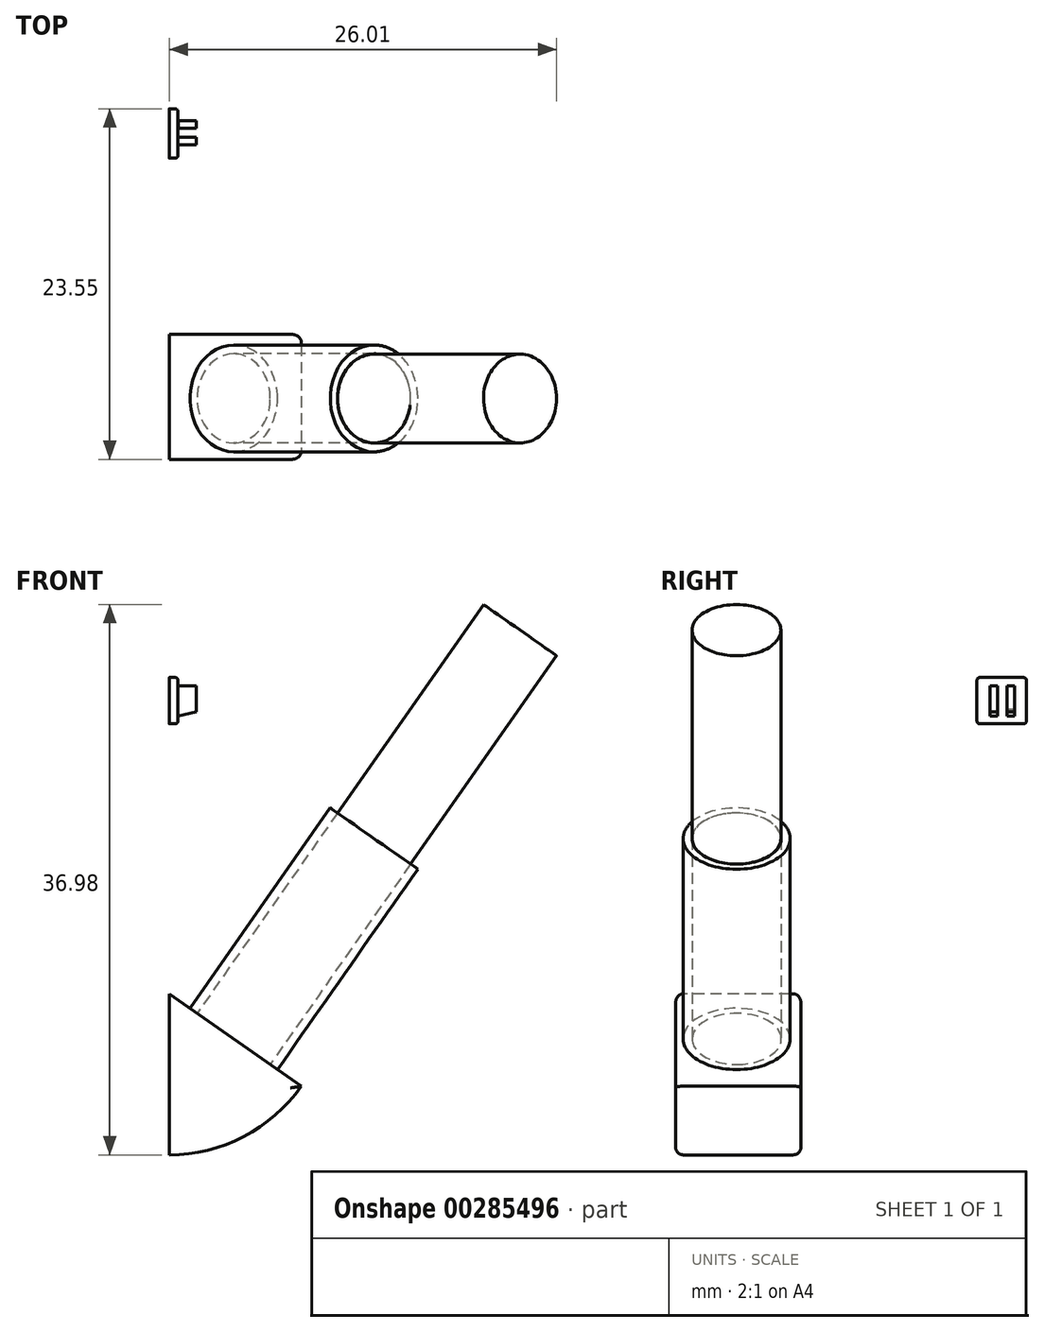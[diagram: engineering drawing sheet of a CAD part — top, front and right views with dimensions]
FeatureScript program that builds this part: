
annotation { "Feature Type Name" : "Feature", "Feature Type Description" : "" }
export const myFeature = defineFeature(function(context is Context, id is Id, definition is map)
    precondition{}
    {
        {
            var Q0;
            Q0=qCreatedBy(makeId("Right.planeOp"),FACE);
            var sketch = newSketch(context, id + "F0", { "sketchPlane" : qUnion([Q0])});
            skLineSegment(sketch, "E0.bottom", {"start": v(-51.68, 34.1) * mm, "end": v(-60.1, 34.1) * mm});
            skLineSegment(sketch, "E0.top", {"start": v(-51.68, 44.92) * mm, "end": v(-60.1, 44.92) * mm});
            skLineSegment(sketch, "E0.left", {"start": v(-51.68, 34.1) * mm, "end": v(-51.68, 44.92) * mm});
            skLineSegment(sketch, "E0.right", {"start": v(-60.1, 34.1) * mm, "end": v(-60.1, 44.92) * mm});
            skPoint(sketch, "E0.middle", {"position": v(-55.89, 39.5) * mm});
            skSolve(sketch);
        }
        {
            var Q0;
            Q0=makeQuery(id+"F0.imprint","IMPRINT",FACE,{"disambiguationData":[TD([[makeQuery(id+"F0.imprint","IMPRINT",EDGE,{"derivedFrom":sQuery(id+"F0.wireOp",EDGE,"E0.bottom")}),-1.0]])]});
            var Q1;
            Q1=sQuery(id+"F0.wireOp",EDGE,"E0.top");
            revolve(context, id + "F1", {"entities" : qUnion([Q0]), "axis" : qUnion([Q1]), "revolveType" : RevolveType.ONE_DIRECTION, "angle" : 55 * degree});
        }
        {
            var Q0;
            Q0=makeQuery(id+"F1.opRevolve","CAP_FACE",FACE,{"disambiguationData":[OSD([sQuery(id+"F0.wireOp",EDGE,"E0.bottom"),sQuery(id+"F0.wireOp",EDGE,"E0.top"),sQuery(id+"F0.wireOp",EDGE,"E0.left"),sQuery(id+"F0.wireOp",EDGE,"E0.right")])],"isStart":false});
            var sketch = newSketch(context, id + "F2", { "sketchPlane" : qUnion([Q0])});
            skCircle(sketch, "E1", {"center": v(-20.48, -55.99) * mm, "radius": 3.59 * mm});
            skCircle(sketch, "E2", {"center": v(-20.48, -55.99) * mm, "radius": 3 * mm});
            skSolve(sketch);
        }
        {
            var Q0;
            Q0=makeQuery(id+"F2.imprint","IMPRINT",FACE,{"disambiguationData":[TD([[makeQuery(id+"F2.imprint","IMPRINT",EDGE,{"derivedFrom":sQuery(id+"F2.wireOp",EDGE,"E1")}),1.0]])]});
            extrude(context, id + "F3", {"entities" : qUnion([Q0]), "operationType" : NewBodyOperationType.ADD, "depth" : 16.43 * mm});
        }
        {
            var Q0;
            Q0=makeQuery(id+"F3.opExtrude","CAP_FACE",FACE,{"disambiguationData":[OSD([sQuery(id+"F2.wireOp",EDGE,"E1"),sQuery(id+"F2.wireOp",EDGE,"E2")])],"isStart":false});
            var sketch = newSketch(context, id + "F4", { "sketchPlane" : qUnion([Q0])});
            skCircle(sketch, "E3", {"center": v(-20.48, -56.01) * mm, "radius": 3 * mm});
            skSolve(sketch);
        }
        {
            var Q0;
            {var subQ0=sQuery(id+"F4.wireOp",EDGE,"E3");var subQ1=makeQuery(id+"F3.opExtrude","CAP_EDGE",EDGE,{"disambiguationData":[OSD([sQuery(id+"F2.wireOp",EDGE,"E2")])],"isStart":false});var subQ2=makeQuery(id+"F4.imprint","INTERSECT",VERTEX,{"disambiguationData":[OD(0.0)],"derivedFrom":[subQ1,subQ0]});Q0=makeQuery(id+"F4.imprint","IMPRINT",FACE,{"disambiguationData":[TD([[makeQuery(id+"F4.imprint","IMPRINT",EDGE,{"disambiguationData":[TD([[subQ2,1.0]])],"derivedFrom":subQ0}),1.0]])]});}
            var Q1;
            Q1=sQuery(id+"F4.wireOp",EDGE,"E3");
            extrude(context, id + "F5", {"entities" : qUnion([Q0]), "surfaceEntities" : qUnion([Q1]), "depth" : 17.1 * mm});
        }
        {
            var Q0;
            Q0=qCreatedBy(makeId("Right.planeOp"),FACE);
            var sketch = newSketch(context, id + "F6", { "sketchPlane" : qUnion([Q0])});
            skCircle(sketch, "E4", {"center": v(-38.2, 64.6) * mm, "radius": 3 * mm});
            skLineSegment(sketch, "E5.bottom", {"start": v(-36.54, 63.05) * mm, "end": v(-39.85, 63.05) * mm});
            skLineSegment(sketch, "E5.top", {"start": v(-36.54, 66.16) * mm, "end": v(-39.85, 66.16) * mm});
            skLineSegment(sketch, "E5.left", {"start": v(-36.54, 63.05) * mm, "end": v(-36.54, 66.16) * mm});
            skLineSegment(sketch, "E5.right", {"start": v(-39.85, 63.05) * mm, "end": v(-39.85, 66.16) * mm});
            skSolve(sketch);
        }
        {
            var Q0;
            Q0=makeQuery(id+"F6.imprint","IMPRINT",FACE,{"disambiguationData":[TD([[makeQuery(id+"F6.imprint","IMPRINT",EDGE,{"derivedFrom":sQuery(id+"F6.wireOp",EDGE,"E5.bottom")}),-1.0]])]});
            extrude(context, id + "F7", {"entities" : qUnion([Q0]), "depth" : 0.58 * mm});
        }
        {
            var Q0;
            Q0=makeQuery(id+"F7.opExtrude","SWEPT_EDGE",EDGE,{"disambiguationData":[OSD([sQuery(id+"F6.wireOp",EDGE,"E5.top"),sQuery(id+"F6.wireOp",EDGE,"E5.right")])]});
            var Q1;
            Q1=makeQuery(id+"F7.opExtrude","SWEPT_EDGE",EDGE,{"disambiguationData":[OSD([sQuery(id+"F6.wireOp",EDGE,"E5.top"),sQuery(id+"F6.wireOp",EDGE,"E5.left")])]});
            var Q2;
            Q2=makeQuery(id+"F7.opExtrude","CAP_FACE",FACE,{"disambiguationData":[OSD([sQuery(id+"F6.wireOp",EDGE,"E5.bottom"),sQuery(id+"F6.wireOp",EDGE,"E5.top"),sQuery(id+"F6.wireOp",EDGE,"E5.left"),sQuery(id+"F6.wireOp",EDGE,"E5.right")])],"isStart":false});
            var Q3;
            Q3=makeQuery(id+"F7.opExtrude","SWEPT_EDGE",EDGE,{"disambiguationData":[OSD([sQuery(id+"F6.wireOp",EDGE,"E5.bottom"),sQuery(id+"F6.wireOp",EDGE,"E5.left")])]});
            var Q4;
            Q4=makeQuery(id+"F7.opExtrude","SWEPT_EDGE",EDGE,{"disambiguationData":[OSD([sQuery(id+"F6.wireOp",EDGE,"E5.bottom"),sQuery(id+"F6.wireOp",EDGE,"E5.right")])]});
            fillet(context, id + "F8", {"entities" : qUnion([Q0, Q1, Q2, Q3, Q4]), "radius" : 0.18 * mm, "tangentPropagation" : true, "allowEdgeOverflow" : false});
        }
        {
            var Q0;
            Q0=makeQuery(id+"F1.opRevolve","SWEPT_EDGE",EDGE,{"disambiguationData":[OSD([sQuery(id+"F0.wireOp",EDGE,"E0.bottom"),sQuery(id+"F0.wireOp",EDGE,"E0.right")])]});
            var Q1;
            Q1=makeQuery(id+"F1.opRevolve","SWEPT_EDGE",EDGE,{"disambiguationData":[OSD([sQuery(id+"F0.wireOp",EDGE,"E0.bottom"),sQuery(id+"F0.wireOp",EDGE,"E0.left")])]});
            var Q2;
            Q2=makeQuery(id+"F1.opRevolve","CAP_EDGE",EDGE,{"disambiguationData":[OSD([sQuery(id+"F0.wireOp",EDGE,"E0.right")])],"isStart":false});
            var Q3;
            Q3=makeQuery(id+"F1.opRevolve","CAP_EDGE",EDGE,{"disambiguationData":[OSD([sQuery(id+"F0.wireOp",EDGE,"E0.left")])],"isStart":false});
            fillet(context, id + "F9", {"entities" : qUnion([Q0, Q1, Q2, Q3]), "radius" : 0.5 * mm, "tangentPropagation" : true, "allowEdgeOverflow" : false});
        }
        {
            var Q0;
            Q0=qCreatedBy(makeId("Front.planeOp"),FACE);
            cPlane(context, id + "F10", {"entities" : qUnion([Q0]), "cplaneType" : CPlaneType.OFFSET, "offset" : 37.6 * mm, "width" : 152.4 * mm, "height" : 152.4 * mm});
        }
        {
            var Q0;
            Q0=qCreatedBy(makeId("Front.planeOp"),FACE);
            cPlane(context, id + "F11", {"entities" : qUnion([Q0]), "cplaneType" : CPlaneType.OFFSET, "offset" : 38.7 * mm, "width" : 152.4 * mm, "height" : 152.4 * mm});
        }
        {
            var Q0;
            Q0=qCreatedBy(id+"F11.planeOp",FACE);
            var sketch = newSketch(context, id + "F12", { "sketchPlane" : qUnion([Q0])});
            skLineSegment(sketch, "E6", {"start": v(0.6, 65.6) * mm, "end": v(1.83, 65.6) * mm});
            skLineSegment(sketch, "E7", {"start": v(1.83, 65.6) * mm, "end": v(1.83, 63.86) * mm});
            skLineSegment(sketch, "E8", {"start": v(1.83, 63.86) * mm, "end": v(0.58, 63.58) * mm});
            skLineSegment(sketch, "E9", {"start": v(0.58, 63.58) * mm, "end": v(0.6, 65.6) * mm});
            skSolve(sketch);
        }
        {
            var Q0;
            Q0=qCreatedBy(id+"F10.planeOp",FACE);
            var sketch = newSketch(context, id + "F13", { "sketchPlane" : qUnion([Q0])});
            skLineSegment(sketch, "E10", {"start": v(0.6, 65.6) * mm, "end": v(1.83, 65.6) * mm});
            skLineSegment(sketch, "E11", {"start": v(1.83, 65.6) * mm, "end": v(1.83, 63.86) * mm});
            skLineSegment(sketch, "E12", {"start": v(1.83, 63.86) * mm, "end": v(0.58, 63.59) * mm});
            skLineSegment(sketch, "E13", {"start": v(0.58, 63.59) * mm, "end": v(0.6, 65.6) * mm});
            skSolve(sketch);
        }
        {
            var Q0;
            Q0=makeQuery(id+"F12.imprint","IMPRINT",FACE,{"disambiguationData":[TD([[makeQuery(id+"F12.imprint","IMPRINT",EDGE,{"derivedFrom":sQuery(id+"F12.wireOp",EDGE,"E6")}),-1.0]])]});
            extrude(context, id + "F14", {"entities" : qUnion([Q0]), "operationType" : NewBodyOperationType.ADD, "endBound" : BoundingType.SYMMETRIC, "depth" : 0.5 * mm});
        }
        {
            var Q0;
            Q0=makeQuery(id+"F13.imprint","IMPRINT",FACE,{"disambiguationData":[TD([[makeQuery(id+"F13.imprint","IMPRINT",EDGE,{"derivedFrom":sQuery(id+"F13.wireOp",EDGE,"E10")}),-1.0]])]});
            extrude(context, id + "F15", {"entities" : qUnion([Q0]), "operationType" : NewBodyOperationType.ADD, "endBound" : BoundingType.SYMMETRIC, "depth" : 0.5 * mm});
        }
    });
